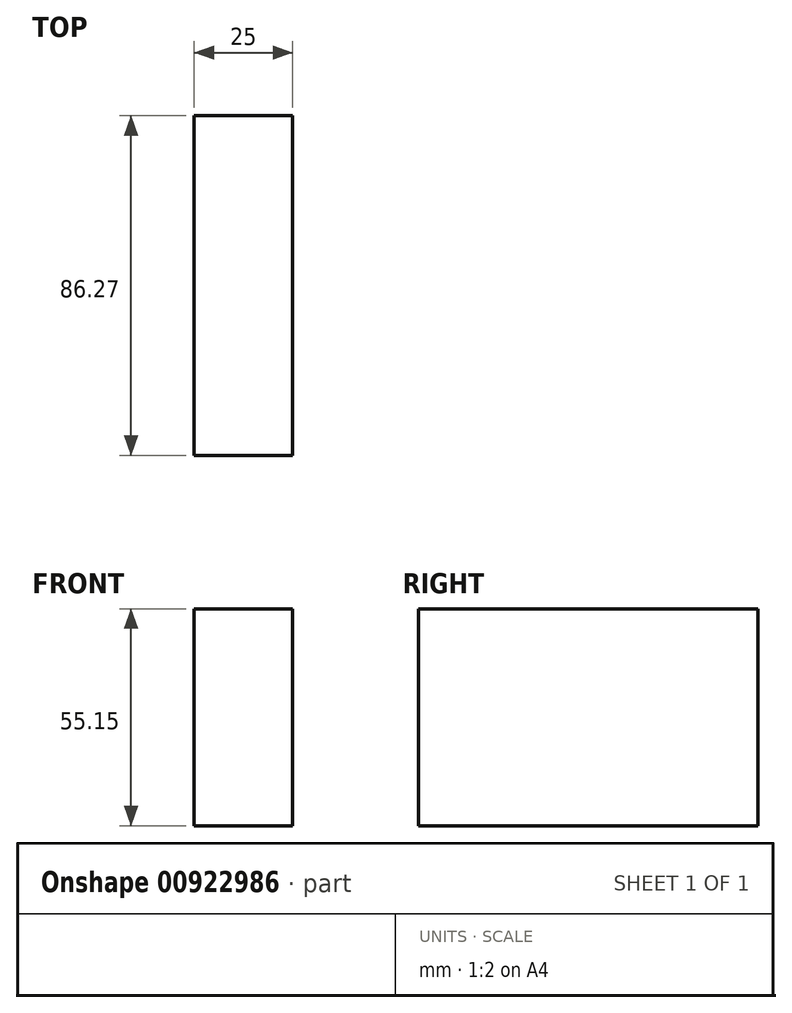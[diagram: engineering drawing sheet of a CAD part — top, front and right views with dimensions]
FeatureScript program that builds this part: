
annotation { "Feature Type Name" : "Feature", "Feature Type Description" : "" }
export const myFeature = defineFeature(function(context is Context, id is Id, definition is map)
    precondition{}
    {
        {
            var Q0;
            Q0=qCreatedBy(makeId("Right.planeOp"),FACE);
            var sketch = newSketch(context, id + "F0", { "sketchPlane" : qUnion([Q0])});
            skLineSegment(sketch, "E0.bottom", {"start": v(37.45, 0) * mm, "end": v(-48.82, 0) * mm});
            skLineSegment(sketch, "E0.top", {"start": v(37.45, -55.15) * mm, "end": v(-48.82, -55.15) * mm});
            skLineSegment(sketch, "E0.left", {"start": v(37.45, 0) * mm, "end": v(37.45, -55.15) * mm});
            skLineSegment(sketch, "E0.right", {"start": v(-48.82, 0) * mm, "end": v(-48.82, -55.15) * mm});
            skSolve(sketch);
        }
        {
            var Q0;
            Q0=makeQuery(id+"F0.imprint","IMPRINT",FACE,{"disambiguationData":[TD([[makeQuery(id+"F0.imprint","IMPRINT",EDGE,{"derivedFrom":sQuery(id+"F0.wireOp",EDGE,"E0.bottom")}),1.0]])]});
            extrude(context, id + "F1", {"entities" : qUnion([Q0]), "depth" : 25 * mm, "offsetDistance" : 25 * mm});
        }
    });
